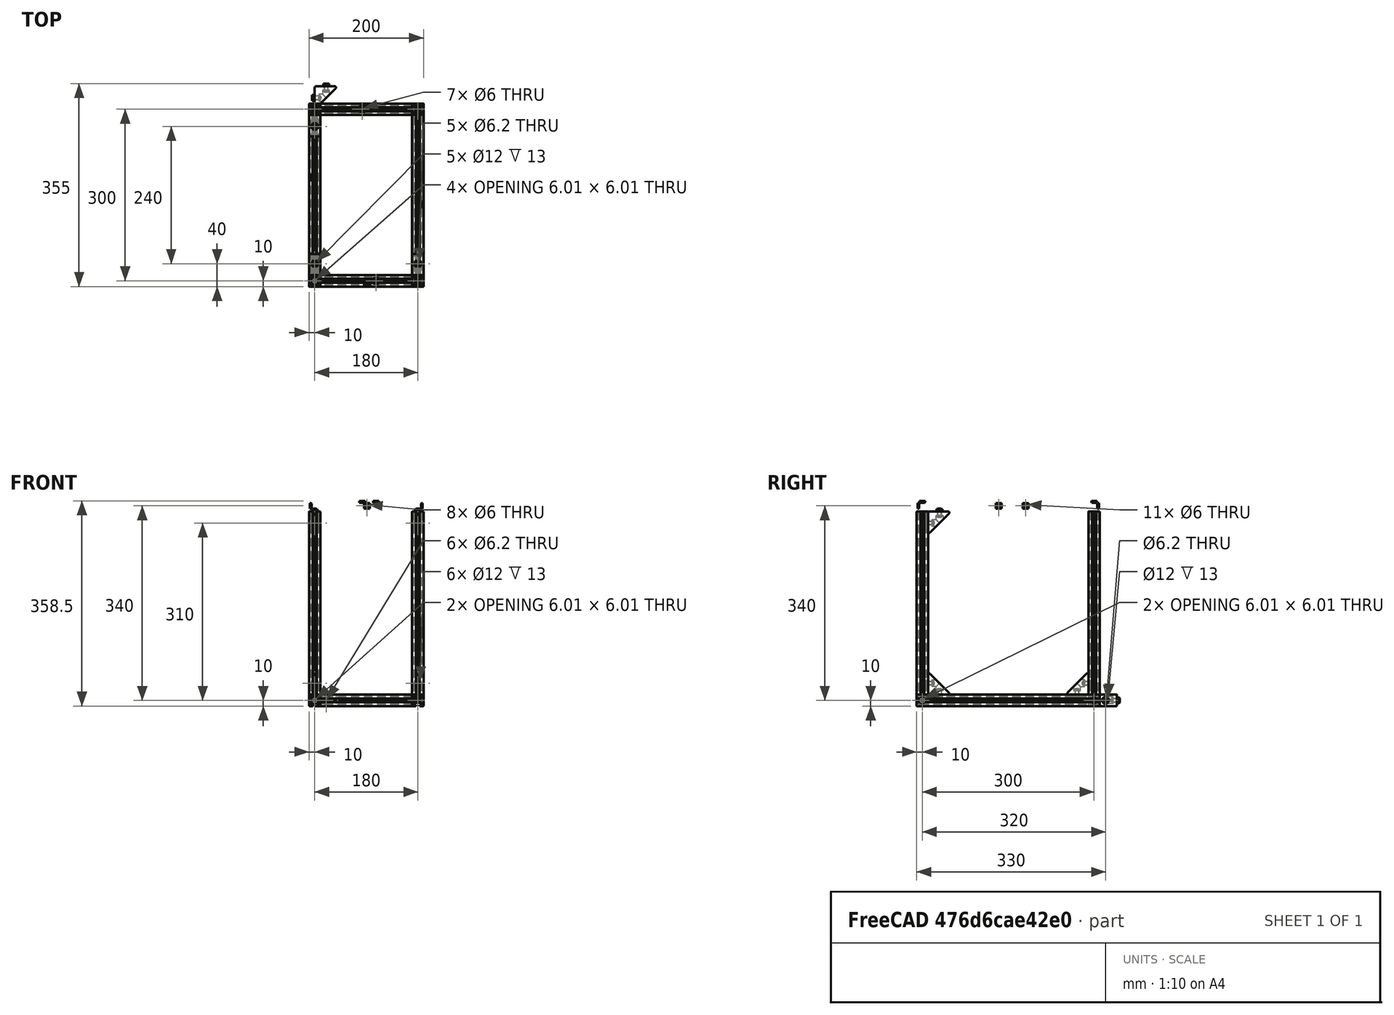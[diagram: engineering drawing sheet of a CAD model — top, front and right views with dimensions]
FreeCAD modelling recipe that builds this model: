
FCSTD DOCUMENT  (FreeCAD 0.17R9796 (Git))
Label: upperframe3
License: All rights reserved
LicenseURL: http://en.wikipedia.org/wiki/All_rights_reserved
objects: Part::Feature×55, Part::FeaturePython×16, App::Part×6, Part::Compound×5
note: 76 computed .brp shape members not serialized (recipe doc carries the construction recipe); baked Part::Feature solids carry a one-line shape summary decoded from their .brp

FEATURE [Part::Feature] Pocket003001  label="tslot32con"
  Placement = pos=(0,10,10) rot=(1,0,0;1.5708rad)
  shape: bbox 20 x 320 x 20 mm, 150 faces (baked)
FEATURE [Part::Feature] Pocket003002  label="tslot16"
  Placement = pos=(10,0,10) rot=(0,1,0;1.5708rad)
  shape: bbox 160 x 20 x 20 mm, 94 faces (baked)
FEATURE [Part::Feature] Pocket003006  label="tslot16_001"
  Placement = pos=(10,-300,10) rot=(0,1,0;1.5708rad)
  shape: bbox 160 x 20 x 20 mm, 94 faces (baked)
FEATURE [Part::Feature] Pocket003007  label="tslot32con_001"
  Placement = pos=(180,-310,10) rot=(0,0.707107,0.707107;3.14159rad)
  shape: bbox 20 x 320 x 20 mm, 150 faces (baked)
FEATURE [Part::FeaturePython] Screw  label="M6x25-Screw"  # Fasteners workbench fastener (typed FeaturePython)
  Placement = pos=(-4,0,10) rot=(0,-1,0;1.5708rad)
  diameter = 7
  invert = false
  length = 6
  matchOuter = false
  offset = 0
  thread = false
  type = 15
FEATURE [Part::FeaturePython] Screw001  label="M6x25-Screw004"  # Fasteners workbench fastener (typed FeaturePython)
  Placement = pos=(-4,-300,10) rot=(0,-1,0;1.5708rad)
  diameter = 7
  invert = false
  length = 6
  matchOuter = false
  offset = 0
  thread = false
  type = 15
FEATURE [Part::FeaturePython] Screw002  label="M6x25-Screw005"  # Fasteners workbench fastener (typed FeaturePython)
  Placement = pos=(184,0,10) rot=(0,1,0;1.5708rad)
  diameter = 7
  invert = false
  length = 6
  matchOuter = false
  offset = 0
  thread = false
  type = 15
FEATURE [Part::FeaturePython] Screw004  label="M6x25-Screw006"  # Fasteners workbench fastener (typed FeaturePython)
  Placement = pos=(184,-300,10) rot=(0,1,0;1.5708rad)
  diameter = 7
  invert = false
  length = 6
  matchOuter = false
  offset = 0
  thread = false
  type = 15
FEATURE [App::Part] Part  label="lower_frame"
  Group = -> [Pocket003001,Pocket003002,Pocket003006,Pocket003007,Screw,Screw001,Screw002,Screw004]
  License = CC BY 3.0
  LicenseURL = http://creativecommons.org/licenses/by/3.0/
  Origin = -> PartOrigin
FEATURE [Part::Feature] Pocket003008  label="tslot32con001"
  Placement = pos=(0,10,10) rot=(1,0,0;1.5708rad)
  shape: bbox 20 x 320 x 20 mm, 150 faces (baked)
FEATURE [Part::Feature] Pocket003009  label="tslot041"
  Placement = pos=(10,0,10) rot=(0,1,0;1.5708rad)
  shape: bbox 160 x 20 x 20 mm, 94 faces (baked)
FEATURE [Part::Feature] Pocket003010  label="tslot16_002"
  Placement = pos=(10,-300,10) rot=(0,1,0;1.5708rad)
  shape: bbox 160 x 20 x 20 mm, 94 faces (baked)
FEATURE [Part::Feature] Pocket003011  label="tslot32con_002"
  Placement = pos=(180,-310,10) rot=(0,0.707107,0.707107;3.14159rad)
  shape: bbox 20 x 320 x 20 mm, 150 faces (baked)
FEATURE [Part::FeaturePython] Screw005  label="M6x25-Screw012"  # Fasteners workbench fastener (typed FeaturePython)
  Placement = pos=(-4,0,10) rot=(0,-1,0;1.5708rad)
  diameter = 7
  invert = false
  length = 6
  matchOuter = false
  offset = 0
  thread = false
  type = 15
FEATURE [Part::FeaturePython] Screw006  label="M6x25-Screw015"  # Fasteners workbench fastener (typed FeaturePython)
  Placement = pos=(-4,-300,10) rot=(0,-1,0;1.5708rad)
  diameter = 7
  invert = false
  length = 6
  matchOuter = false
  offset = 0
  thread = false
  type = 15
FEATURE [Part::FeaturePython] Screw007  label="M6x25-Screw017"  # Fasteners workbench fastener (typed FeaturePython)
  Placement = pos=(184,0,10) rot=(0,1,0;1.5708rad)
  diameter = 7
  invert = false
  length = 6
  matchOuter = false
  offset = 0
  thread = false
  type = 15
FEATURE [Part::FeaturePython] Screw008  label="M6x25-Screw016"  # Fasteners workbench fastener (typed FeaturePython)
  Placement = pos=(184,-300,10) rot=(0,1,0;1.5708rad)
  diameter = 7
  invert = false
  length = 6
  matchOuter = false
  offset = 0
  thread = false
  type = 15
FEATURE [App::Part] Part001  label="upper_frame"
  Group = -> [Pocket003008,Pocket003009,Pocket003010,Pocket003011,Screw005,Screw006,Screw007,Screw008]
  License = CC BY 3.0
  LicenseURL = http://creativecommons.org/licenses/by/3.0/
  Origin = -> PartOrigin001
  Placement = pos=(0,0,340) rot=(0,0,1;0rad)
FEATURE [Part::Feature] Fillet004001  label="Fillet005"
  shape: bbox 37.5 x 37.5 x 20 mm, 26 faces (baked)
FEATURE [Part::FeaturePython] Screw009  label="M6x12-Screw"  # Fasteners workbench fastener (typed FeaturePython)
  Placement = pos=(7,20,10) rot=(0,1,0;1.5708rad)
  diameter = 4
  invert = false
  length = 1
  matchOuter = false
  offset = 0
  thread = false
  type = 20
FEATURE [Part::Feature] Body001  label="m6nutplate"
  Placement = pos=(-1.5,15,5) rot=(0,-1,0;1.5708rad)
  shape: bbox 3 x 10 x 10 mm, 9 faces (baked)
FEATURE [App::Part] Part002  label="cornerstonescrewnut"
  License = CC BY 3.0
  LicenseURL = http://creativecommons.org/licenses/by/3.0/
  Origin = -> PartOrigin002
  Placement = pos=(10,-50,20) rot=(0,-1,0;1.5708rad)
FEATURE [Part::FeaturePython] Screw010  label="M6x12-Screw001"  # Fasteners workbench fastener (typed FeaturePython)
  Placement = pos=(20,33,10) rot=(1,0,0;1.5708rad)
  diameter = 4
  invert = false
  length = 1
  matchOuter = false
  offset = 0
  thread = false
  type = 20
FEATURE [Part::Feature] Body002  label="m6nutplate001"
  Placement = pos=(15,41.5,5) rot=(0.57735,0.57735,0.57735;4.18879rad)
  shape: bbox 10 x 3 x 10 mm, 9 faces (baked)
FEATURE [Part::Feature] Fillet004002  label="Fillet006"
  shape: bbox 37.5 x 37.5 x 20 mm, 26 faces (baked)
FEATURE [Part::FeaturePython] Screw011  label="M6x12-Screw002"  # Fasteners workbench fastener (typed FeaturePython)
  Placement = pos=(7,20,10) rot=(0,1,0;1.5708rad)
  diameter = 4
  invert = false
  length = 1
  matchOuter = false
  offset = 0
  thread = false
  type = 20
FEATURE [Part::Feature] Body003  label="m6nutplate002"
  Placement = pos=(-1.5,15,5) rot=(0,-1,0;1.5708rad)
  shape: bbox 3 x 10 x 10 mm, 9 faces (baked)
FEATURE [Part::FeaturePython] Screw012  label="M6x12-Screw003"  # Fasteners workbench fastener (typed FeaturePython)
  Placement = pos=(20,33,10) rot=(1,0,0;1.5708rad)
  diameter = 4
  invert = false
  length = 1
  matchOuter = false
  offset = 0
  thread = false
  type = 20
FEATURE [Part::Feature] Body004  label="m6nutplate003"
  Placement = pos=(15,41.5,5) rot=(0.57735,0.57735,0.57735;4.18879rad)
  shape: bbox 10 x 3 x 10 mm, 9 faces (baked)
FEATURE [App::Part] Part003  label="cornerstonescrewnut001"
  Group = -> [Body003,Screw011,Fillet004002,Screw012,Body004,PartOrigin002,Body001,Screw009,Fillet004001,Screw010,Body002,Part002]
  License = CC BY 3.0
  LicenseURL = http://creativecommons.org/licenses/by/3.0/
  Origin = -> PartOrigin003
  Placement = pos=(190,-50,20) rot=(0,-1,0;1.5708rad)
FEATURE [Part::Feature] Fillet004003  label="Fillet007"
  shape: bbox 37.5 x 37.5 x 20 mm, 26 faces (baked)
FEATURE [Part::FeaturePython] Screw013  label="M6x12-Screw004"  # Fasteners workbench fastener (typed FeaturePython)
  Placement = pos=(7,20,10) rot=(0,1,0;1.5708rad)
  diameter = 4
  invert = false
  length = 1
  matchOuter = false
  offset = 0
  thread = false
  type = 20
FEATURE [Part::Feature] Body005  label="m6nutplate004"
  Placement = pos=(-1.5,15,5) rot=(0,-1,0;1.5708rad)
  shape: bbox 3 x 10 x 10 mm, 9 faces (baked)
FEATURE [Part::FeaturePython] Screw014  label="M6x12-Screw005"  # Fasteners workbench fastener (typed FeaturePython)
  Placement = pos=(20,33,10) rot=(1,0,0;1.5708rad)
  diameter = 4
  invert = false
  length = 1
  matchOuter = false
  offset = 0
  thread = false
  type = 20
FEATURE [Part::Feature] Body006  label="m6nutplate005"
  Placement = pos=(15,41.5,5) rot=(0.57735,0.57735,0.57735;4.18879rad)
  shape: bbox 10 x 3 x 10 mm, 9 faces (baked)
FEATURE [App::Part] Part004  label="cornerstonescrewnut002"
  Group = -> [Body005,Screw013,Fillet004003,Screw014,Body006]
  License = CC BY 3.0
  LicenseURL = http://creativecommons.org/licenses/by/3.0/
  Origin = -> PartOrigin004
  Placement = pos=(-10,-50,340) rot=(0,1,0;1.5708rad)
FEATURE [Part::Feature] Fillet004004  label="Fillet008"
  shape: bbox 37.5 x 37.5 x 20 mm, 26 faces (baked)
FEATURE [Part::FeaturePython] Screw015  label="M6x12-Screw006"  # Fasteners workbench fastener (typed FeaturePython)
  Placement = pos=(7,20,10) rot=(0,1,0;1.5708rad)
  diameter = 4
  invert = false
  length = 1
  matchOuter = false
  offset = 0
  thread = false
  type = 20
FEATURE [Part::Feature] Body007  label="m6nutplate006"
  Placement = pos=(-1.5,15,5) rot=(0,-1,0;1.5708rad)
  shape: bbox 3 x 10 x 10 mm, 9 faces (baked)
FEATURE [Part::FeaturePython] Screw016  label="M6x12-Screw007"  # Fasteners workbench fastener (typed FeaturePython)
  Placement = pos=(20,33,10) rot=(1,0,0;1.5708rad)
  diameter = 4
  invert = false
  length = 1
  matchOuter = false
  offset = 0
  thread = false
  type = 20
FEATURE [Part::Feature] Body008  label="m6nutplate007"
  Placement = pos=(15,41.5,5) rot=(0.57735,0.57735,0.57735;4.18879rad)
  shape: bbox 10 x 3 x 10 mm, 9 faces (baked)
FEATURE [App::Part] Part005  label="cornerstonescrewnut003"
  Group = -> [Body007,Screw015,Fillet004004,Screw016,Body008]
  License = CC BY 3.0
  LicenseURL = http://creativecommons.org/licenses/by/3.0/
  Origin = -> PartOrigin005
  Placement = pos=(170,-50,340) rot=(0,1,0;1.5708rad)
FEATURE [Part::Feature] Body009001  label="m6nutplate010"
  Placement = pos=(-1.5,15,5) rot=(0,-1,0;1.5708rad)
  shape: bbox 3 x 10 x 10 mm, 9 faces (baked)
FEATURE [Part::Feature] Body010001  label="m6nutplate011"
  Placement = pos=(15,41.5,5) rot=(0.57735,0.57735,0.57735;4.18879rad)
  shape: bbox 10 x 3 x 10 mm, 9 faces (baked)
FEATURE [Part::Feature] Screw018001  label="M6x12-Screw010"
  Placement = pos=(20,33,10) rot=(1,0,0;1.5708rad)
  shape: bbox 10.5 x 15.3 x 10.5 mm, 15 faces (baked)
FEATURE [Part::Feature] Screw017001  label="M6x12-Screw011"
  Placement = pos=(7,20,10) rot=(0,1,0;1.5708rad)
  shape: bbox 15.3 x 10.5 x 10.5 mm, 15 faces (baked)
FEATURE [Part::Feature] Fillet004005001  label="Fillet010"
  shape: bbox 37.5 x 37.5 x 20 mm, 26 faces (baked)
FEATURE [Part::Compound] Compound
  Links = -> [Body009001,Fillet004005001,Screw017001,Body010001,Screw018001]
  Placement = pos=(10,-250,340) rot=(0.707107,0,-0.707107;3.14159rad)
FEATURE [Part::Feature] Body010002  label="m6nutplate012"
  Placement = pos=(-1.5,15,5) rot=(0,-1,0;1.5708rad)
  shape: bbox 3 x 10 x 10 mm, 9 faces (baked)
FEATURE [Part::Feature] Body010003  label="m6nutplate013"
  Placement = pos=(15,41.5,5) rot=(0.57735,0.57735,0.57735;4.18879rad)
  shape: bbox 10 x 3 x 10 mm, 9 faces (baked)
FEATURE [Part::Feature] Screw018002  label="M6x12-Screw012"
  Placement = pos=(20,33,10) rot=(1,0,0;1.5708rad)
  shape: bbox 10.5 x 15.3 x 10.5 mm, 15 faces (baked)
FEATURE [Part::Feature] Screw018003  label="M6x12-Screw013"
  Placement = pos=(7,20,10) rot=(0,1,0;1.5708rad)
  shape: bbox 15.3 x 10.5 x 10.5 mm, 15 faces (baked)
FEATURE [Part::Feature] Fillet004005002  label="Fillet011"
  shape: bbox 37.5 x 37.5 x 20 mm, 26 faces (baked)
FEATURE [Part::Compound] Compound001
  Links = -> [Body010002,Fillet004005002,Screw018003,Body010003,Screw018002]
  Placement = pos=(190,-250,340) rot=(0.707107,0,-0.707107;3.14159rad)
FEATURE [Part::Feature] Body010004  label="m6nutplate014"
  Placement = pos=(-1.5,15,5) rot=(0,-1,0;1.5708rad)
  shape: bbox 3 x 10 x 10 mm, 9 faces (baked)
FEATURE [Part::Feature] Body010005  label="m6nutplate015"
  Placement = pos=(15,41.5,5) rot=(0.57735,0.57735,0.57735;4.18879rad)
  shape: bbox 10 x 3 x 10 mm, 9 faces (baked)
FEATURE [Part::Feature] Screw018004  label="M6x12-Screw014"
  Placement = pos=(20,33,10) rot=(1,0,0;1.5708rad)
  shape: bbox 10.5 x 15.3 x 10.5 mm, 15 faces (baked)
FEATURE [Part::Feature] Screw018005  label="M6x12-Screw015"
  Placement = pos=(7,20,10) rot=(0,1,0;1.5708rad)
  shape: bbox 15.3 x 10.5 x 10.5 mm, 15 faces (baked)
FEATURE [Part::Feature] Fillet004005003  label="Fillet012"
  shape: bbox 37.5 x 37.5 x 20 mm, 26 faces (baked)
FEATURE [Part::Compound] Compound002
  Links = -> [Body010004,Fillet004005003,Screw018005,Body010005,Screw018004]
  Placement = pos=(10,-290,60) rot=(0.57735,0.57735,-0.57735;4.18879rad)
FEATURE [Part::Feature] Body010006  label="m6nutplate016"
  Placement = pos=(-1.5,15,5) rot=(0,-1,0;1.5708rad)
  shape: bbox 3 x 10 x 10 mm, 9 faces (baked)
FEATURE [Part::Feature] Body010007  label="m6nutplate017"
  Placement = pos=(15,41.5,5) rot=(0.57735,0.57735,0.57735;4.18879rad)
  shape: bbox 10 x 3 x 10 mm, 9 faces (baked)
FEATURE [Part::Feature] Screw018006  label="M6x12-Screw016"
  Placement = pos=(20,33,10) rot=(1,0,0;1.5708rad)
  shape: bbox 10.5 x 15.3 x 10.5 mm, 15 faces (baked)
FEATURE [Part::Feature] Screw018007  label="M6x12-Screw017"
  Placement = pos=(7,20,10) rot=(0,1,0;1.5708rad)
  shape: bbox 15.3 x 10.5 x 10.5 mm, 15 faces (baked)
FEATURE [Part::Feature] Fillet004005004  label="Fillet013"
  shape: bbox 37.5 x 37.5 x 20 mm, 26 faces (baked)
FEATURE [Part::Compound] Compound003
  Links = -> [Body010006,Fillet004005004,Screw018007,Body010007,Screw018006]
  Placement = pos=(190,-290,60) rot=(0.57735,0.57735,-0.57735;4.18879rad)
FEATURE [Part::Feature] Pocket001001  label="tslot32"
  Placement = pos=(0,0,20) rot=(0,0,1;0rad)
  shape: bbox 20 x 20 x 320 mm, 94 faces (baked)
FEATURE [Part::Feature] Body010008  label="m6nutplate018"
  Placement = pos=(-1.5,15,5) rot=(0,-1,0;1.5708rad)
  shape: bbox 3 x 10 x 10 mm, 9 faces (baked)
FEATURE [Part::Feature] Body010009  label="m6nutplate019"
  Placement = pos=(15,41.5,5) rot=(0.57735,0.57735,0.57735;4.18879rad)
  shape: bbox 10 x 3 x 10 mm, 9 faces (baked)
FEATURE [Part::Feature] Screw018008  label="M6x12-Screw018"
  Placement = pos=(20,33,10) rot=(1,0,0;1.5708rad)
  shape: bbox 10.5 x 15.3 x 10.5 mm, 15 faces (baked)
FEATURE [Part::Feature] Screw018009  label="M6x12-Screw019"
  Placement = pos=(7,20,10) rot=(0,1,0;1.5708rad)
  shape: bbox 15.3 x 10.5 x 10.5 mm, 15 faces (baked)
FEATURE [Part::Feature] Fillet004005005  label="Fillet014"
  shape: bbox 37.5 x 37.5 x 20 mm, 26 faces (baked)
FEATURE [Part::Compound] Compound004
  Links = -> [Body010008,Fillet004005005,Screw018009,Body010009,Screw018008]
  Placement = pos=(-10,-10,60) rot=(0.57735,-0.57735,0.57735;4.18879rad)
FEATURE [Part::Feature] Pocket003012  label="tslot32_001"
  Placement = pos=(0,-300,20) rot=(0,0,1;0rad)
  shape: bbox 20 x 20 x 320 mm, 94 faces (baked)
FEATURE [Part::Feature] Pocket003013  label="tslot32_002"
  Placement = pos=(180,0,20) rot=(0,0,1;0rad)
  shape: bbox 20 x 20 x 320 mm, 94 faces (baked)
FEATURE [Part::Feature] Pocket003014  label="tslot32_003"
  Placement = pos=(180,-300,20) rot=(0,0,1;0rad)
  shape: bbox 20 x 20 x 320 mm, 94 faces (baked)
FEATURE [Part::Feature] Chamfer001001  label="m6nutplate020"
  Placement = pos=(112,-295,358.5) rot=(0.707107,-0.707107,0;3.14159rad)
  shape: bbox 10 x 10 x 3 mm, 9 faces (baked)
FEATURE [Part::Feature] Chamfer001002  label="m6nutplate021"
  Placement = pos=(96,-308.5,355) rot=(0.57735,-0.57735,-0.57735;4.18879rad)
  shape: bbox 10 x 3 x 10 mm, 9 faces (baked)
FEATURE [Part::Feature] Chamfer001003  label="m6nutplate022"
  Placement = pos=(-8.5,-124.5,355) rot=(0,1,0;1.5708rad)
  shape: bbox 3 x 10 x 10 mm, 9 faces (baked)
FEATURE [Part::Feature] Chamfer001004  label="m6nutplate023"
  Placement = pos=(88,5,358.5) rot=(0.707107,-0.707107,0;3.14159rad)
  shape: bbox 10 x 10 x 3 mm, 9 faces (baked)
FEATURE [Part::Feature] Chamfer001005  label="m6nutplate024"
  Placement = pos=(96,8.5,345) rot=(0.57735,-0.57735,0.57735;2.0944rad)
  shape: bbox 10 x 3 x 10 mm, 9 faces (baked)
FEATURE [Part::Feature] Chamfer001006  label="m6nutplate025"
  Placement = pos=(188.5,-171.5,345) rot=(0,1,0;4.71239rad)
  shape: bbox 3 x 10 x 10 mm, 9 faces (baked)
